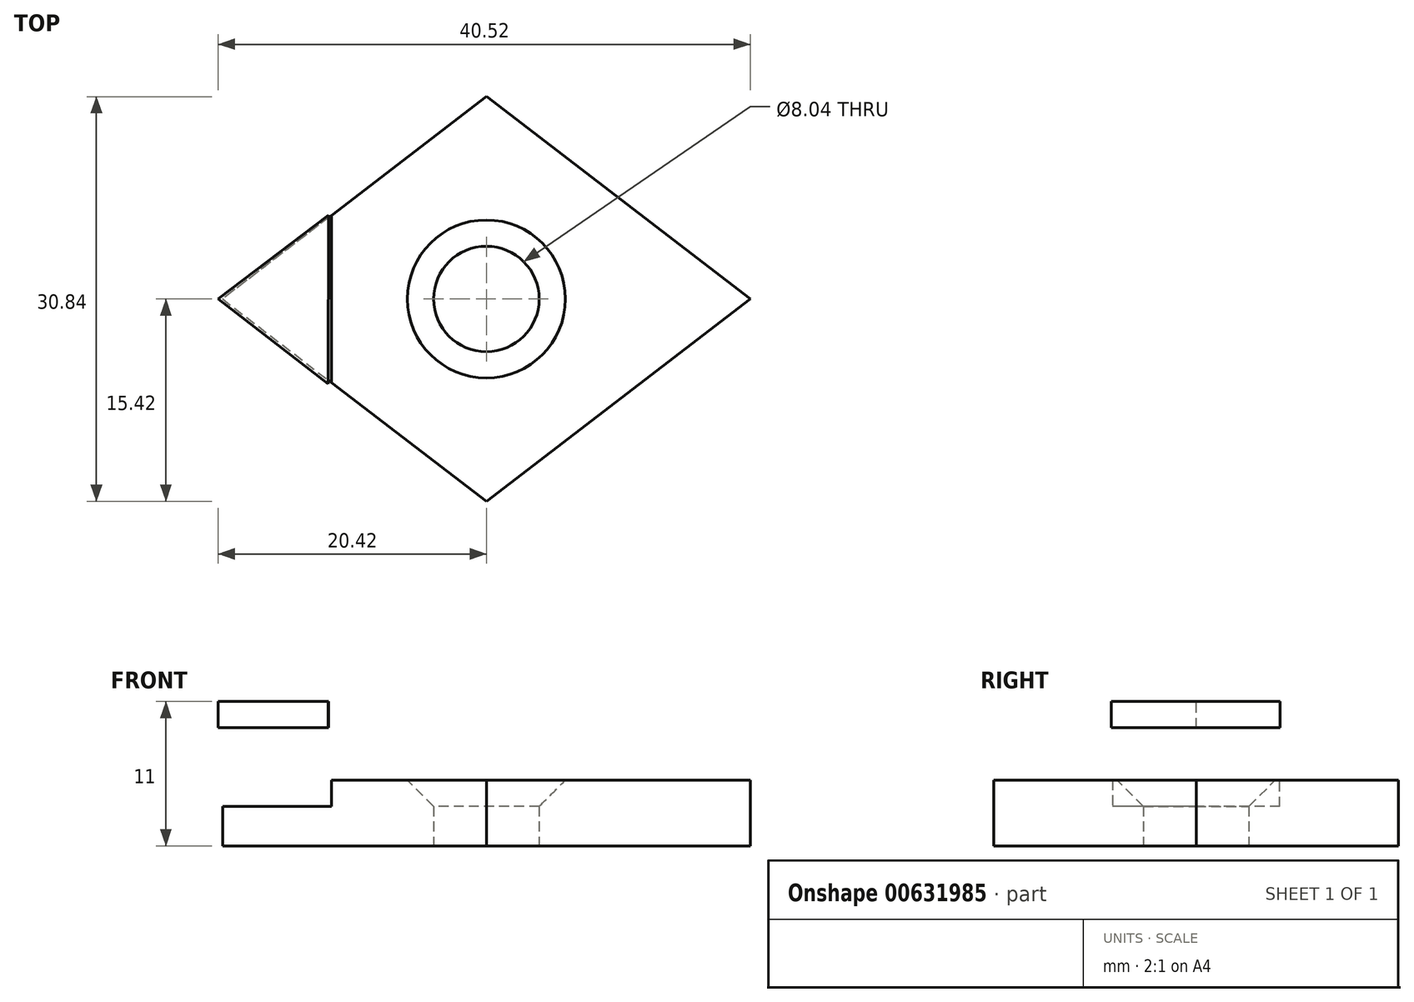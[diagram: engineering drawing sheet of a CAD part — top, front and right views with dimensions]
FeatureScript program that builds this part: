
annotation { "Feature Type Name" : "Feature", "Feature Type Description" : "" }
export const myFeature = defineFeature(function(context is Context, id is Id, definition is map)
    precondition{}
    {
        {
            var Q0;
            Q0=qCreatedBy(makeId("Top.planeOp"),FACE);
            var sketch = newSketch(context, id + "F0", { "sketchPlane" : qUnion([Q0])});
            skLineSegment(sketch, "E0", {"start": v(20.1, 0) * mm, "end": v(0, 15.42) * mm});
            skLineSegment(sketch, "E1", {"start": v(20.1, 0) * mm, "end": v(0, -15.42) * mm});
            skLineSegment(sketch, "E2", {"start": v(0, 15.42) * mm, "end": v(-20.1, 0) * mm});
            skLineSegment(sketch, "E3", {"start": v(-20.1, 0) * mm, "end": v(0, -15.42) * mm});
            skCircle(sketch, "E4", {"center": v(0, 0) * mm, "radius": 4.02 * mm});
            skSolve(sketch);
        }
        {
            var Q0;
            Q0 = qSketchRegion(id + "F0", true);
            extrude(context, id + "F1", {"entities" : qUnion([Q0]), "depth" : 5 * mm, "offsetDistance" : 25 * mm});
        }
        {
            var Q0;
            Q0=makeQuery(id+"F1.opExtrude","CAP_EDGE",EDGE,{"disambiguationData":[OSD([sQuery(id+"F0.wireOp",EDGE,"E4")])],"isStart":false});
            chamfer(context, id + "F2", {"entities" : qUnion([Q0]), "width" : 2 * mm, "tangentPropagation" : true});
        }
        {
            var Q0;
            Q0=qCreatedBy(makeId("Top.planeOp"),FACE);
            cPlane(context, id + "F3", {"entities" : qUnion([Q0]), "cplaneType" : CPlaneType.OFFSET, "offset" : 3 * mm, "width" : 150 * mm, "height" : 150 * mm});
        }
        {
            var Q0;
            Q0=qCreatedBy(id+"F3.planeOp",FACE);
            var sketch = newSketch(context, id + "F4", { "sketchPlane" : qUnion([Q0])});
            skLineSegment(sketch, "E5", {"start": v(-20.53, 0) * mm, "end": v(-11.8, 6.7) * mm});
            skLineSegment(sketch, "E6", {"start": v(-11.8, 6.7) * mm, "end": v(-11.8, -6.7) * mm});
            skLineSegment(sketch, "E7", {"start": v(-11.8, -6.7) * mm, "end": v(-20.53, 0) * mm});
            skSolve(sketch);
        }
        {
            var Q0;
            Q0 = qSketchRegion(id + "F4", true);
            extrude(context, id + "F5", {"entities" : qUnion([Q0]), "operationType" : NewBodyOperationType.REMOVE, "depth" : 25 * mm, "offsetDistance" : 25 * mm});
        }
        {
            var Q0;
            Q0=qCreatedBy(id+"F3.planeOp",FACE);
            cPlane(context, id + "F6", {"entities" : qUnion([Q0]), "cplaneType" : CPlaneType.OFFSET, "offset" : 8 * mm, "width" : 150 * mm, "height" : 150 * mm});
        }
        {
            var Q0;
            Q0=qCreatedBy(id+"F6.planeOp",FACE);
            var sketch = newSketch(context, id + "F7", { "sketchPlane" : qUnion([Q0])});
            skLineSegment(sketch, "E8", {"start": v(-12.02, 6.4) * mm, "end": v(-20.42, 0) * mm});
            skLineSegment(sketch, "E9", {"start": v(-20.42, 0) * mm, "end": v(-12.06, -6.46) * mm});
            skLineSegment(sketch, "E10", {"start": v(-12.02, 6.4) * mm, "end": v(-12.06, -6.46) * mm});
            skSolve(sketch);
        }
        {
            var Q0;
            Q0 = qSketchRegion(id + "F7", true);
            extrude(context, id + "F8", {"entities" : qUnion([Q0]), "oppositeDirection" : true, "depth" : 2 * mm, "offsetDistance" : 25 * mm});
        }
    });
